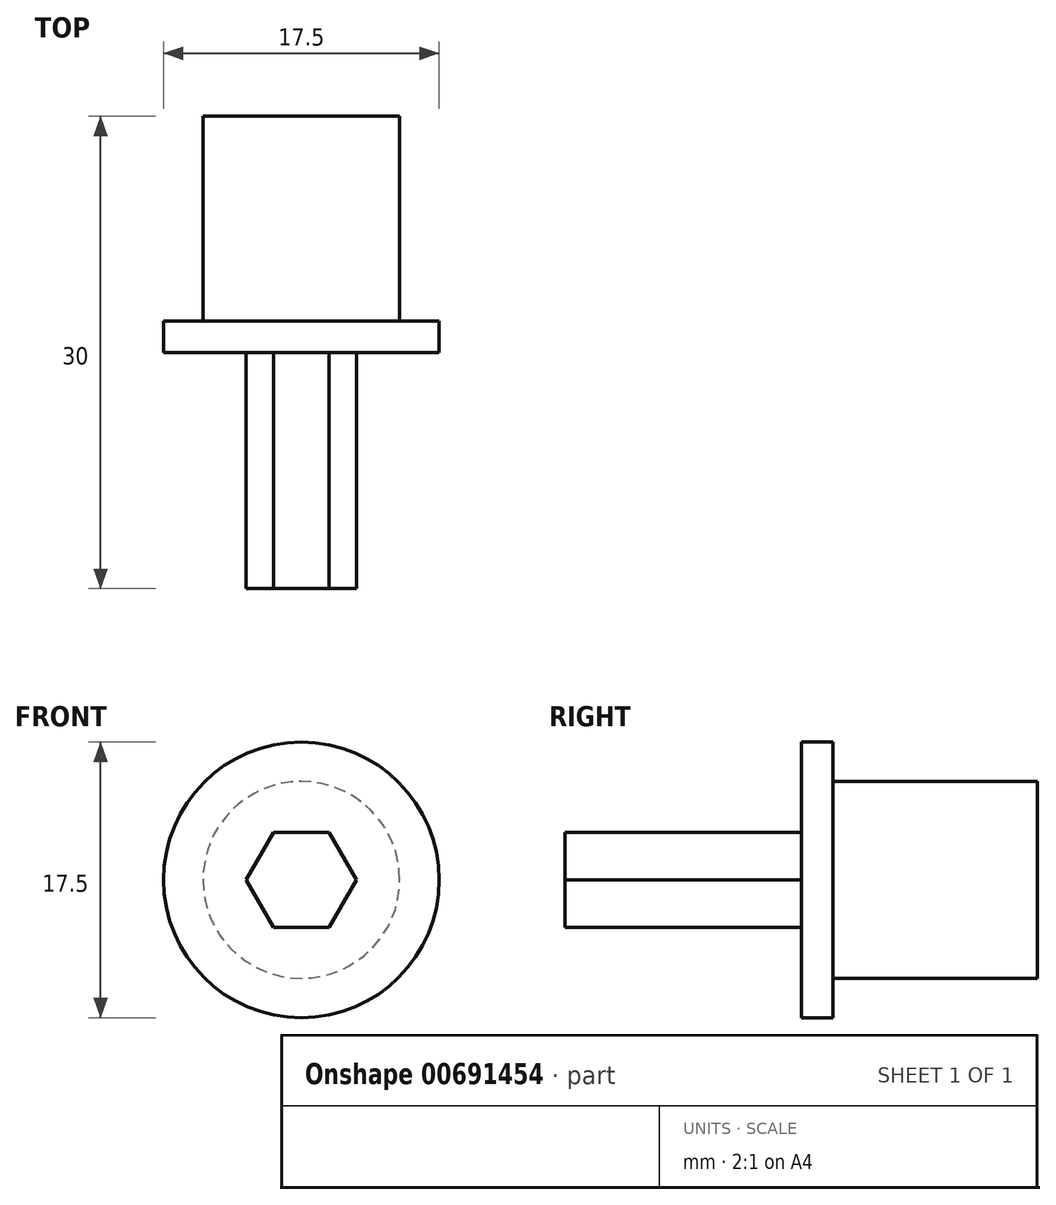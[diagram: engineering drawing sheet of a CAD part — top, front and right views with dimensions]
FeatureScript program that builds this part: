
annotation { "Feature Type Name" : "Feature", "Feature Type Description" : "" }
export const myFeature = defineFeature(function(context is Context, id is Id, definition is map)
    precondition{}
    {
        {
            var Q0;
            Q0=qCreatedBy(makeId("Front.planeOp"),FACE);
            var sketch = newSketch(context, id + "F0", { "sketchPlane" : qUnion([Q0])});
            skCircle(sketch, "E0", {"center": v(0, 0) * mm, "radius": 8.75 * mm});
            skCircle(sketch, "E1", {"center": v(0, 0) * mm, "radius": 6.25 * mm});
            skCircle(sketch, "E2.cCircle", {"center": v(0, 0) * mm, "radius": 3.03 * mm, "construction": true});
            skLineSegment(sketch, "E2.0", {"start": v(-1.75, -3.03) * mm, "end": v(-3.5, 0) * mm});
            skLineSegment(sketch, "E2.1", {"start": v(-3.5, 0) * mm, "end": v(-1.75, 3.03) * mm});
            skLineSegment(sketch, "E2.2", {"start": v(-1.75, 3.03) * mm, "end": v(1.75, 3.03) * mm});
            skLineSegment(sketch, "E2.3", {"start": v(1.75, 3.03) * mm, "end": v(3.5, 0) * mm});
            skLineSegment(sketch, "E2.4", {"start": v(3.5, 0) * mm, "end": v(1.75, -3.03) * mm});
            skLineSegment(sketch, "E2.5", {"start": v(1.75, -3.03) * mm, "end": v(-1.75, -3.03) * mm});
            skPoint(sketch, "E2.0.midPoint", {"position": v(-2.62, -1.52) * mm});
            skSolve(sketch);
        }
        {
            var Q0;
            Q0=makeQuery(id+"F0.imprint","IMPRINT",FACE,{"disambiguationData":[TD([[makeQuery(id+"F0.imprint","IMPRINT",EDGE,{"derivedFrom":sQuery(id+"F0.wireOp",EDGE,"E0")}),1.0]])]});
            extrude(context, id + "F1", {"entities" : qUnion([Q0]), "oppositeDirection" : true, "depth" : 2 * mm, "offsetDistance" : 25 * mm});
        }
        {
            var Q0;
            Q0=makeQuery(id+"F0.imprint","IMPRINT",FACE,{"disambiguationData":[TD([[makeQuery(id+"F0.imprint","IMPRINT",EDGE,{"derivedFrom":sQuery(id+"F0.wireOp",EDGE,"E1")}),1.0]])]});
            extrude(context, id + "F2", {"entities" : qUnion([Q0]), "operationType" : NewBodyOperationType.ADD, "oppositeDirection" : true, "depth" : 15 * mm, "offsetDistance" : 25 * mm});
        }
        {
            var Q0;
            Q0=makeQuery(id+"F0.imprint","IMPRINT",FACE,{"disambiguationData":[TD([[makeQuery(id+"F0.imprint","IMPRINT",EDGE,{"derivedFrom":sQuery(id+"F0.wireOp",EDGE,"E2.0")}),-1.0]])]});
            extrude(context, id + "F3", {"entities" : qUnion([Q0]), "operationType" : NewBodyOperationType.ADD, "endBound" : BoundingType.SYMMETRIC, "depth" : 30 * mm, "offsetDistance" : 25 * mm});
        }
    });
